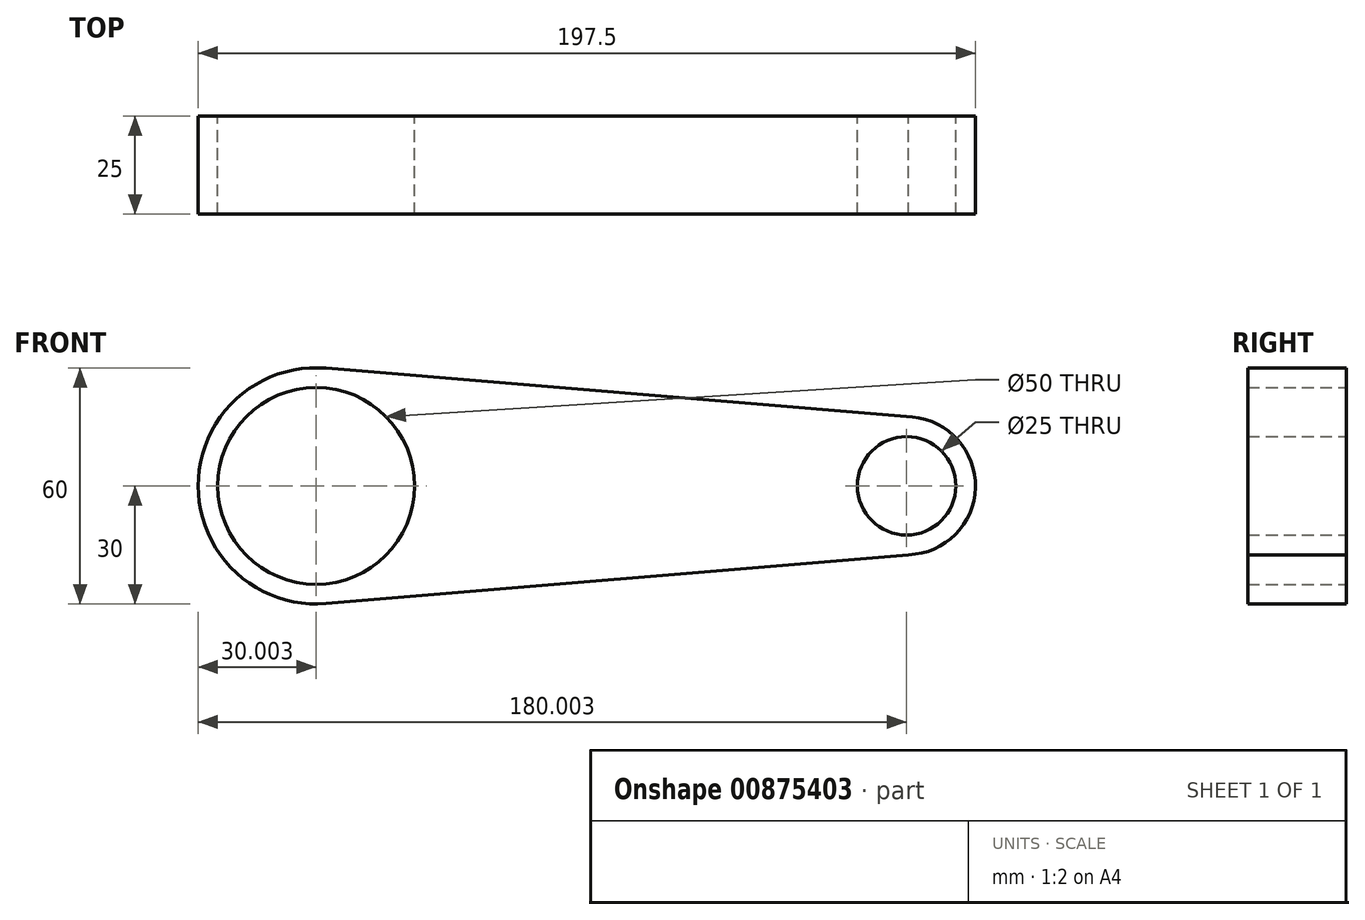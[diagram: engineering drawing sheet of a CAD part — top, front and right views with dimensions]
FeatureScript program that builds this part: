
annotation { "Feature Type Name" : "Feature", "Feature Type Description" : "" }
export const myFeature = defineFeature(function(context is Context, id is Id, definition is map)
    precondition{}
    {
        {
            var Q0;
            Q0=qCreatedBy(makeId("Front.planeOp"),FACE);
            var sketch = newSketch(context, id + "F0", { "sketchPlane" : qUnion([Q0])});
            skCircle(sketch, "E0", {"center": v(-89.15, 0) * mm, "radius": 25 * mm});
            skCircle(sketch, "E1", {"center": v(60.85, 0) * mm, "radius": 12.5 * mm});
            skCircle(sketch, "E2", {"center": v(-89.15, 0) * mm, "radius": 30 * mm});
            skCircle(sketch, "E3", {"center": v(60.85, 0) * mm, "radius": 17.5 * mm});
            skLineSegment(sketch, "E4", {"start": v(-86.65, 29.9) * mm, "end": v(62.31, 17.44) * mm});
            skLineSegment(sketch, "E5", {"start": v(61.37, -17.5) * mm, "end": v(-86.64, -29.9) * mm});
            skSolve(sketch);
        }
        {
            var Q0;
            Q0 = qSketchRegion(id + "F0", true);
            extrude(context, id + "F1", {"entities" : qUnion([Q0]), "depth" : 25 * mm, "offsetDistance" : 25 * mm});
        }
    });
